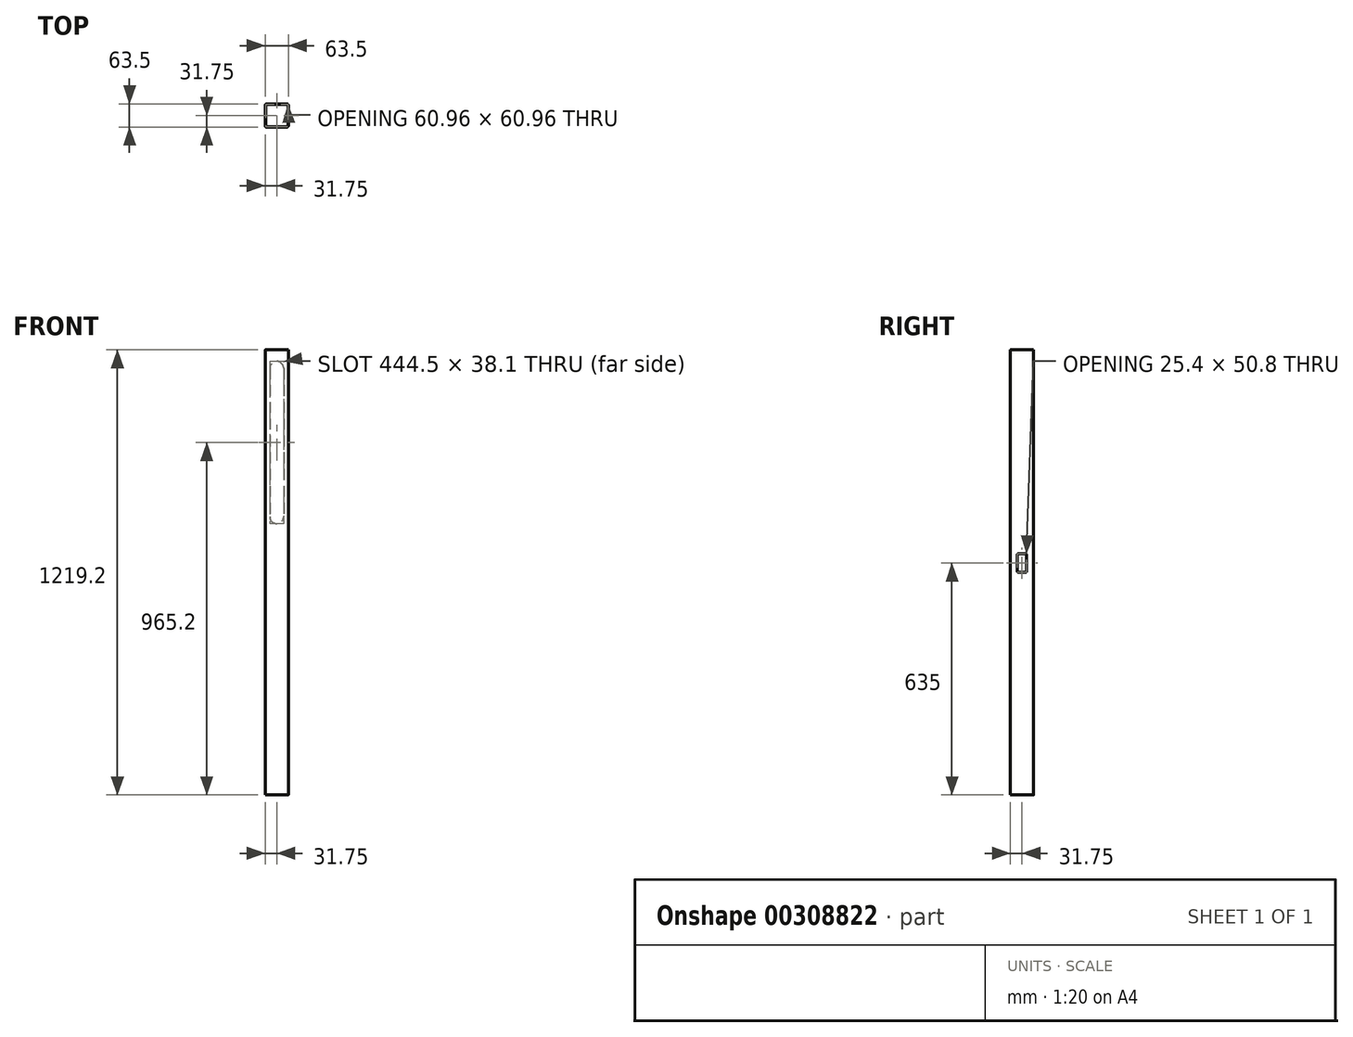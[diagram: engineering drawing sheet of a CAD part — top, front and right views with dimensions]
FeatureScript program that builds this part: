
annotation { "Feature Type Name" : "Feature", "Feature Type Description" : "" }
export const myFeature = defineFeature(function(context is Context, id is Id, definition is map)
    precondition{}
    {
        {
            var Q0;
            Q0=qCreatedBy(makeId("Top.planeOp"),FACE);
            var sketch = newSketch(context, id + "F0", { "sketchPlane" : qUnion([Q0])});
            skLineSegment(sketch, "E0.bottom", {"start": v(27.94, 31.75) * mm, "end": v(-27.94, 31.75) * mm});
            skLineSegment(sketch, "E0.top", {"start": v(27.94, -31.75) * mm, "end": v(-27.94, -31.75) * mm});
            skLineSegment(sketch, "E0.left", {"start": v(31.75, 27.94) * mm, "end": v(31.75, -27.94) * mm});
            skLineSegment(sketch, "E0.right", {"start": v(-31.75, 27.94) * mm, "end": v(-31.75, -27.94) * mm});
            skPoint(sketch, "E0.middle", {"position": v(0, 0) * mm});
            skLineSegment(sketch, "E1.bottom", {"start": v(26.67, 30.48) * mm, "end": v(-26.67, 30.48) * mm});
            skLineSegment(sketch, "E1.top", {"start": v(26.67, -30.48) * mm, "end": v(-26.67, -30.48) * mm});
            skLineSegment(sketch, "E1.left", {"start": v(30.48, 26.67) * mm, "end": v(30.48, -26.67) * mm});
            skLineSegment(sketch, "E1.right", {"start": v(-30.48, 26.67) * mm, "end": v(-30.48, -26.67) * mm});
            skPoint(sketch, "E2.visualSharp", {"position": v(-30.48, 30.48) * mm});
            skArc(sketch, "E2.filletArc", {"start": v(-26.67, 30.48) * mm, "mid": v(-29.36, 29.36) * mm, "end": v(-30.48, 26.67) * mm});
            skPoint(sketch, "E3.visualSharp", {"position": v(-31.75, 31.75) * mm});
            skArc(sketch, "E3.filletArc", {"start": v(-27.94, 31.75) * mm, "mid": v(-30.63, 30.63) * mm, "end": v(-31.75, 27.94) * mm});
            skPoint(sketch, "E4.visualSharp", {"position": v(30.48, 30.48) * mm});
            skArc(sketch, "E4.filletArc", {"start": v(30.48, 26.67) * mm, "mid": v(29.36, 29.36) * mm, "end": v(26.67, 30.48) * mm});
            skPoint(sketch, "E5.visualSharp", {"position": v(31.75, 31.75) * mm});
            skArc(sketch, "E5.filletArc", {"start": v(31.75, 27.94) * mm, "mid": v(30.63, 30.63) * mm, "end": v(27.94, 31.75) * mm});
            skPoint(sketch, "E6.visualSharp", {"position": v(31.75, -31.75) * mm});
            skArc(sketch, "E6.filletArc", {"start": v(27.94, -31.75) * mm, "mid": v(30.63, -30.63) * mm, "end": v(31.75, -27.94) * mm});
            skPoint(sketch, "E7.visualSharp", {"position": v(30.48, -30.48) * mm});
            skArc(sketch, "E7.filletArc", {"start": v(26.67, -30.48) * mm, "mid": v(29.36, -29.36) * mm, "end": v(30.48, -26.67) * mm});
            skPoint(sketch, "E8.visualSharp", {"position": v(-30.48, -30.48) * mm});
            skArc(sketch, "E8.filletArc", {"start": v(-30.48, -26.67) * mm, "mid": v(-29.36, -29.36) * mm, "end": v(-26.67, -30.48) * mm});
            skPoint(sketch, "E9.visualSharp", {"position": v(-31.75, -31.75) * mm});
            skArc(sketch, "E9.filletArc", {"start": v(-31.75, -27.94) * mm, "mid": v(-30.63, -30.63) * mm, "end": v(-27.94, -31.75) * mm});
            skSolve(sketch);
        }
        {
            var Q0;
            Q0 = qSketchRegion(id + "F0", true);
            extrude(context, id + "F1", {"entities" : qUnion([Q0]), "depth" : 1219.2 * mm});
        }
        {
            var Q0;
            Q0=makeQuery(id+"F1.opExtrude","SWEPT_FACE",FACE,{"disambiguationData":[OSD([sQuery(id+"F0.wireOp",EDGE,"E0.bottom")])]});
            var sketch = newSketch(context, id + "F2", { "sketchPlane" : qUnion([Q0])});
            skLineSegment(sketch, "E10", {"start": v(0, 1168.4) * mm, "end": v(0, 762) * mm});
            skArc(sketch, "E11.0.startCap", {"start": v(-19.05, 1168.4) * mm, "mid": v(0, 1187.45) * mm, "end": v(19.05, 1168.4) * mm});
            skArc(sketch, "E11.0.endCap", {"start": v(19.05, 762) * mm, "mid": v(0, 742.95) * mm, "end": v(-19.05, 762) * mm});
            skLineSegment(sketch, "E11.0.left", {"start": v(19.05, 1168.4) * mm, "end": v(19.05, 762) * mm});
            skLineSegment(sketch, "E11.0.right", {"start": v(-19.05, 1168.4) * mm, "end": v(-19.05, 762) * mm});
            skSolve(sketch);
        }
        {
            var Q0;
            Q0 = qSketchRegion(id + "F2", true);
            extrude(context, id + "F3", {"entities" : qUnion([Q0]), "operationType" : NewBodyOperationType.REMOVE, "endBound" : BoundingType.UP_TO_NEXT, "oppositeDirection" : true, "depth" : 25.4 * mm});
        }
        {
            var Q0;
            Q0=makeQuery(id+"F1.opExtrude","SWEPT_FACE",FACE,{"disambiguationData":[OSD([sQuery(id+"F0.wireOp",EDGE,"E0.left")])]});
            var sketch = newSketch(context, id + "F4", { "sketchPlane" : qUnion([Q0])});
            skLineSegment(sketch, "E12.bottom", {"start": v(10.16, 660.4) * mm, "end": v(-10.16, 660.4) * mm});
            skLineSegment(sketch, "E12.top", {"start": v(10.16, 609.6) * mm, "end": v(-10.16, 609.6) * mm});
            skLineSegment(sketch, "E12.left", {"start": v(12.7, 657.86) * mm, "end": v(12.7, 612.14) * mm});
            skLineSegment(sketch, "E12.right", {"start": v(-12.7, 657.86) * mm, "end": v(-12.7, 612.14) * mm});
            skPoint(sketch, "E12.middle", {"position": v(0, 635) * mm});
            skPoint(sketch, "E13.visualSharp", {"position": v(-12.7, 660.4) * mm});
            skArc(sketch, "E13.filletArc", {"start": v(-10.16, 660.4) * mm, "mid": v(-11.96, 659.66) * mm, "end": v(-12.7, 657.86) * mm});
            skPoint(sketch, "E14.visualSharp", {"position": v(12.7, 660.4) * mm});
            skArc(sketch, "E14.filletArc", {"start": v(12.7, 657.86) * mm, "mid": v(11.96, 659.66) * mm, "end": v(10.16, 660.4) * mm});
            skPoint(sketch, "E15.visualSharp", {"position": v(12.7, 609.6) * mm});
            skArc(sketch, "E15.filletArc", {"start": v(10.16, 609.6) * mm, "mid": v(11.96, 610.34) * mm, "end": v(12.7, 612.14) * mm});
            skPoint(sketch, "E16.visualSharp", {"position": v(-12.7, 609.6) * mm});
            skArc(sketch, "E16.filletArc", {"start": v(-12.7, 612.14) * mm, "mid": v(-11.96, 610.34) * mm, "end": v(-10.16, 609.6) * mm});
            skSolve(sketch);
        }
        {
            var Q0;
            Q0 = qSketchRegion(id + "F4", true);
            extrude(context, id + "F5", {"entities" : qUnion([Q0]), "operationType" : NewBodyOperationType.REMOVE, "endBound" : BoundingType.UP_TO_NEXT, "oppositeDirection" : true, "depth" : 25.4 * mm});
        }
    });
